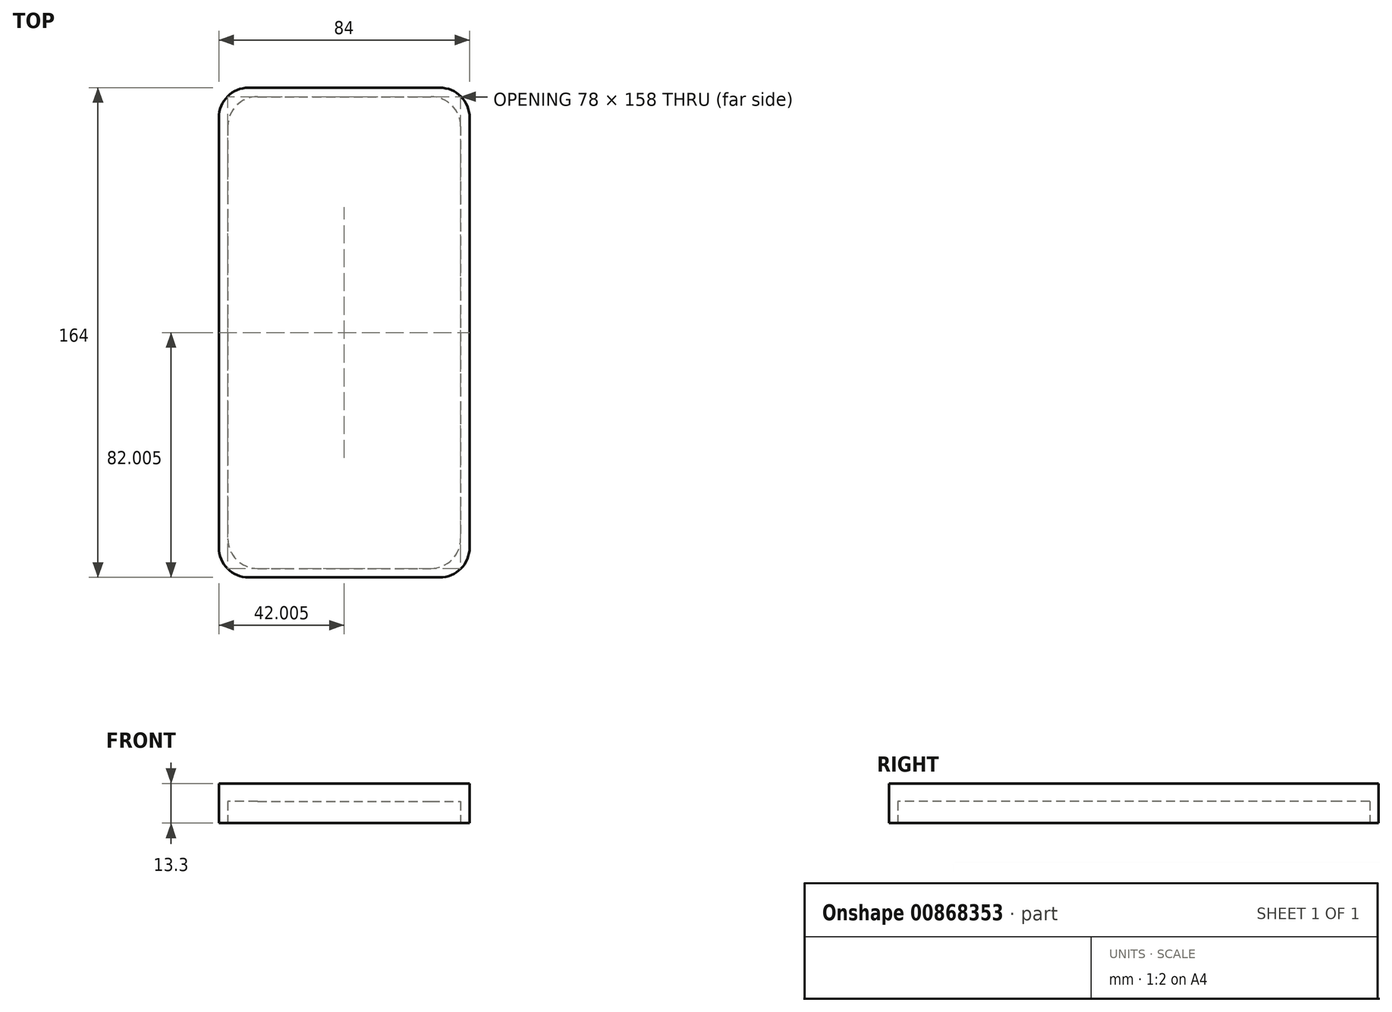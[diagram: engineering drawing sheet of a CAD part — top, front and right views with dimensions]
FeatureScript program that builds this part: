
annotation { "Feature Type Name" : "Feature", "Feature Type Description" : "" }
export const myFeature = defineFeature(function(context is Context, id is Id, definition is map)
    precondition{}
    {
        {
            var Q0;
            Q0=qCreatedBy(makeId("Top.planeOp"),FACE);
            var sketch = newSketch(context, id + "F0", { "sketchPlane" : qUnion([Q0])});
            skLineSegment(sketch, "E0.bottom", {"start": v(-28.9, 81.7) * mm, "end": v(35.1, 81.7) * mm});
            skLineSegment(sketch, "E0.top", {"start": v(-28.9, -82.3) * mm, "end": v(35.1, -82.3) * mm});
            skLineSegment(sketch, "E0.left", {"start": v(-38.9, 71.7) * mm, "end": v(-38.9, -72.3) * mm});
            skLineSegment(sketch, "E0.right", {"start": v(45.1, 71.7) * mm, "end": v(45.1, -72.3) * mm});
            skPoint(sketch, "E1.visualSharp", {"position": v(45.1, 81.7) * mm});
            skArc(sketch, "E1.filletArc", {"start": v(45.1, 71.7) * mm, "mid": v(42.18, 78.77) * mm, "end": v(35.1, 81.7) * mm});
            skPoint(sketch, "E2.visualSharp", {"position": v(-38.9, 81.7) * mm});
            skArc(sketch, "E2.filletArc", {"start": v(-28.9, 81.7) * mm, "mid": v(-35.97, 78.77) * mm, "end": v(-38.9, 71.7) * mm});
            skPoint(sketch, "E3.visualSharp", {"position": v(45.1, -82.3) * mm});
            skArc(sketch, "E3.filletArc", {"start": v(35.1, -82.3) * mm, "mid": v(42.18, -79.38) * mm, "end": v(45.1, -72.3) * mm});
            skPoint(sketch, "E4.visualSharp", {"position": v(-38.9, -82.3) * mm});
            skArc(sketch, "E4.filletArc", {"start": v(-38.9, -72.3) * mm, "mid": v(-35.97, -79.38) * mm, "end": v(-28.9, -82.3) * mm});
            skSolve(sketch);
        }
        {
            var Q0;
            Q0 = qSketchRegion(id + "F0", true);
            extrude(context, id + "F1", {"entities" : qUnion([Q0]), "depth" : 13.3 * mm, "offsetDistance" : 25 * mm});
        }
        {
            var Q0;
            Q0=qCreatedBy(makeId("Top.planeOp"),FACE);
            var sketch = newSketch(context, id + "F2", { "sketchPlane" : qUnion([Q0])});
            skLineSegment(sketch, "E5.bottom", {"start": v(-25.9, 78.7) * mm, "end": v(32.1, 78.7) * mm});
            skLineSegment(sketch, "E5.top", {"start": v(-25.9, -79.3) * mm, "end": v(32.1, -79.3) * mm});
            skLineSegment(sketch, "E5.left", {"start": v(-35.9, 68.7) * mm, "end": v(-35.9, -69.3) * mm});
            skLineSegment(sketch, "E5.right", {"start": v(42.1, 68.7) * mm, "end": v(42.1, -69.3) * mm});
            skPoint(sketch, "E6.visualSharp", {"position": v(42.1, 78.7) * mm});
            skArc(sketch, "E6.filletArc", {"start": v(42.1, 68.7) * mm, "mid": v(39.18, 75.77) * mm, "end": v(32.1, 78.7) * mm});
            skPoint(sketch, "E7.visualSharp", {"position": v(-35.9, 78.7) * mm});
            skArc(sketch, "E7.filletArc", {"start": v(-25.9, 78.7) * mm, "mid": v(-32.97, 75.77) * mm, "end": v(-35.9, 68.7) * mm});
            skPoint(sketch, "E8.visualSharp", {"position": v(-35.9, -79.3) * mm});
            skArc(sketch, "E8.filletArc", {"start": v(-35.9, -69.3) * mm, "mid": v(-32.97, -76.38) * mm, "end": v(-25.9, -79.3) * mm});
            skPoint(sketch, "E9.visualSharp", {"position": v(42.1, -79.3) * mm});
            skArc(sketch, "E9.filletArc", {"start": v(32.1, -79.3) * mm, "mid": v(39.18, -76.38) * mm, "end": v(42.1, -69.3) * mm});
            skSolve(sketch);
        }
        {
            var Q0;
            Q0 = qSketchRegion(id + "F2", true);
            extrude(context, id + "F3", {"entities" : qUnion([Q0]), "operationType" : NewBodyOperationType.REMOVE, "depth" : 7.3 * mm, "offsetDistance" : 25 * mm});
        }
    });
